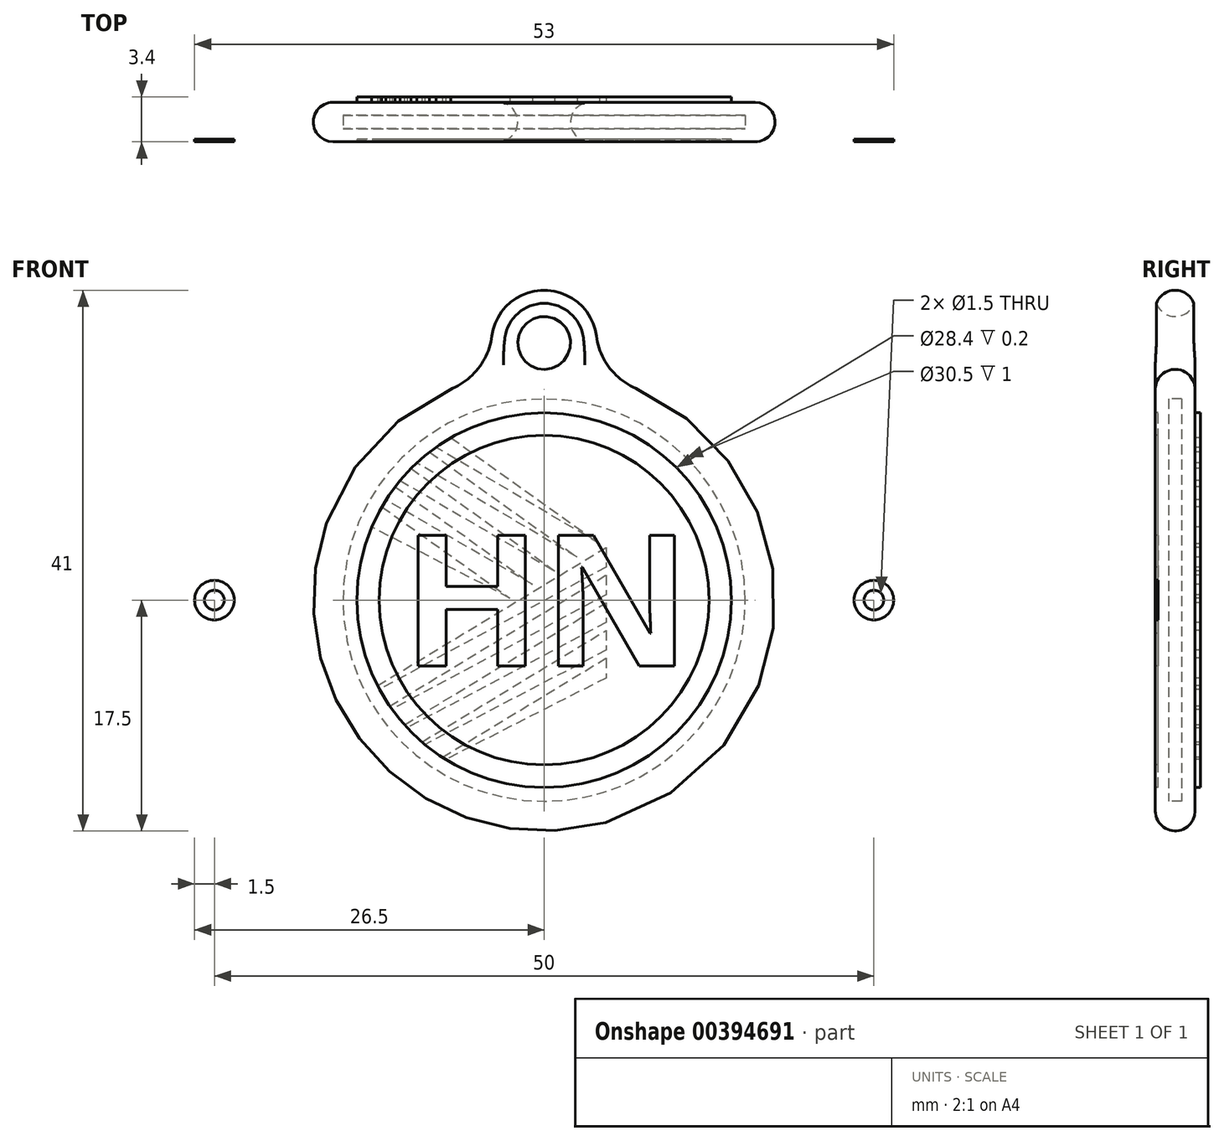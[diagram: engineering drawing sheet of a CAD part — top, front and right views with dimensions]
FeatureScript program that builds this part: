
annotation { "Feature Type Name" : "Feature", "Feature Type Description" : "" }
export const myFeature = defineFeature(function(context is Context, id is Id, definition is map)
    precondition{}
    {
        {
            var Q0;
            Q0=qCreatedBy(makeId("Front.planeOp"),FACE);
            var sketch = newSketch(context, id + "F0", { "sketchPlane" : qUnion([Q0])});
            skCircle(sketch, "E0", {"center": v(0, 0) * mm, "radius": 17.5 * mm});
            skSolve(sketch);
        }
        {
            var Q0;
            Q0 = qSketchRegion(id + "F0", true);
            extrude(context, id + "F1", {"entities" : qUnion([Q0]), "depth" : 1 * mm});
        }
        {
            var Q0;
            Q0=makeQuery(id+"F1.opExtrude","CAP_FACE",FACE,{"disambiguationData":[OSD([sQuery(id+"F0.wireOp",EDGE,"E0")])],"isStart":true});
            var sketch = newSketch(context, id + "F2", { "sketchPlane" : qUnion([Q0])});
            skCircle(sketch, "E1", {"center": v(0, 0) * mm, "radius": 17.5 * mm});
            skCircle(sketch, "E2", {"center": v(0, 0) * mm, "radius": 15.25 * mm});
            skSolve(sketch);
        }
        {
            var Q0;
            Q0 = qSketchRegion(id + "F2", true);
            extrude(context, id + "F3", {"entities" : qUnion([Q0]), "operationType" : NewBodyOperationType.ADD, "depth" : 1 * mm});
        }
        {
            var Q0;
            Q0=makeQuery(id+"F3.opExtrude","CAP_FACE",FACE,{"disambiguationData":[OSD([sQuery(id+"F2.wireOp",EDGE,"E1"),sQuery(id+"F2.wireOp",EDGE,"E2")])],"isStart":false});
            var sketch = newSketch(context, id + "F4", { "sketchPlane" : qUnion([Q0])});
            skCircle(sketch, "E3", {"center": v(0, 0) * mm, "radius": 17.5 * mm});
            skSolve(sketch);
        }
        {
            var Q0;
            Q0 = qSketchRegion(id + "F4", true);
            extrude(context, id + "F5", {"entities" : qUnion([Q0]), "operationType" : NewBodyOperationType.ADD, "depth" : 1 * mm});
        }
        {
            var Q0;
            Q0=makeQuery(id+"F1.opExtrude","CAP_FACE",FACE,{"disambiguationData":[OSD([sQuery(id+"F0.wireOp",EDGE,"E0")])],"isStart":false});
            var sketch = newSketch(context, id + "F6", { "sketchPlane" : qUnion([Q0])});
            skText(sketch, "E4", { "text": "HN", "fontName": "OpenSans-Bold.ttf"});
            skCircle(sketch, "E5", {"center": v(0, 0) * mm, "radius": 12.5 * mm});
            skCircle(sketch, "E6", {"center": v(0, 0) * mm, "radius": 14.2 * mm});
            const initialGuessF6  = {"E4": [-0.01079, -0.005, 1, 0, 0.01]};
            skSetInitialGuess(sketch, initialGuessF6);
            skSolve(sketch);
        }
        {
            var Q0;
            Q0=makeQuery(id+"F6.imprint","IMPRINT",FACE,{"disambiguationData":[TD([[makeQuery(id+"F6.imprint","IMPRINT",EDGE,{"derivedFrom":sQuery(id+"F6.wireOp",EDGE,"E5")}),-1.0]])]});
            var Q1;
            Q1=makeQuery(id+"F6.imprint","IMPRINT",FACE,{"disambiguationData":[TD([[makeQuery(id+"F6.imprint","IMPRINT",EDGE,{"derivedFrom":sQuery(id+"F6.wireOp",EDGE,"E4.sketch_text.stroke-0")}),-1.0]])]});
            var Q2;
            Q2=makeQuery(id+"F6.imprint","IMPRINT",FACE,{"disambiguationData":[TD([[makeQuery(id+"F6.imprint","IMPRINT",EDGE,{"derivedFrom":sQuery(id+"F6.wireOp",EDGE,"E4.sketch_text.stroke-12")}),-1.0]])]});
            var Q3;
            Q3=makeQuery(id+"F6.imprint","IMPRINT",FACE,{"disambiguationData":[TD([[makeQuery(id+"F6.imprint","IMPRINT",EDGE,{"derivedFrom":sQuery(id+"F6.wireOp",EDGE,"E4.sketch_text.stroke-20")}),-1.0]])]});
            var Q4;
            Q4=makeQuery(id+"F6.imprint","IMPRINT",FACE,{"disambiguationData":[TD([[makeQuery(id+"F6.imprint","IMPRINT",EDGE,{"derivedFrom":sQuery(id+"F6.wireOp",EDGE,"E4.sketch_text.stroke-34")}),-1.0]])]});
            var Q5;
            Q5=makeQuery(id+"F6.imprint","IMPRINT",FACE,{"disambiguationData":[TD([[makeQuery(id+"F6.imprint","IMPRINT",EDGE,{"derivedFrom":sQuery(id+"F6.wireOp",EDGE,"2f791306-b3d7-45ab-86ae-8695a74e6aea.sketch_text.stroke-0")}),-1.0]])]});
            var Q6;
            Q6=makeQuery(id+"F6.imprint","IMPRINT",FACE,{"disambiguationData":[TD([[makeQuery(id+"F6.imprint","IMPRINT",EDGE,{"derivedFrom":sQuery(id+"F6.wireOp",EDGE,"2f791306-b3d7-45ab-86ae-8695a74e6aea.sketch_text.stroke-10")}),-1.0]])]});
            var Q7;
            Q7=makeQuery(id+"F6.imprint","IMPRINT",FACE,{"disambiguationData":[TD([[makeQuery(id+"F6.imprint","IMPRINT",EDGE,{"derivedFrom":sQuery(id+"F6.wireOp",EDGE,"2f791306-b3d7-45ab-86ae-8695a74e6aea.sketch_text.stroke-14")}),-1.0]])]});
            var Q8;
            Q8=makeQuery(id+"F6.imprint","IMPRINT",FACE,{"disambiguationData":[TD([[makeQuery(id+"F6.imprint","IMPRINT",EDGE,{"derivedFrom":sQuery(id+"F6.wireOp",EDGE,"2f791306-b3d7-45ab-86ae-8695a74e6aea.sketch_text.stroke-30")}),-1.0]])]});
            extrude(context, id + "F7", {"entities" : qUnion([Q0, Q1, Q2, Q3, Q4, Q5, Q6, Q7, Q8]), "operationType" : NewBodyOperationType.REMOVE, "oppositeDirection" : true, "depth" : 0.2 * mm});
        }
        {
            var Q0;
            Q0=makeQuery(id+"F7.boolean.opBoolean","COPY",FACE,{"derivedFrom":makeQuery(id+"F7.opExtrude","CAP_FACE",FACE,{"disambiguationData":[OSD([sQuery(id+"F6.wireOp",EDGE,"E5"),sQuery(id+"F6.wireOp",EDGE,"E6")])],"isStart":false})});
            var sketch = newSketch(context, id + "F8", { "sketchPlane" : qUnion([Q0])});
            skCircle(sketch, "E7", {"center": v(0, 0) * mm, "radius": 16.5 * mm});
            skCircle(sketch, "E8", {"center": v(0, 0) * mm, "radius": 15 * mm});
            skText(sketch, "E9", { "text": "VIP", "fontName": "OpenSans-Bold.ttf"});
            skText(sketch, "E10", { "text": "H.N.", "fontName": "OpenSans-Bold.ttf"});
            const initialGuessF8  = {"E9": [-0.00735, 0.0025, 1, 0, 0.0065], "E10": [-0.00973, -0.009, 1, 0, 0.0065]};
            skSetInitialGuess(sketch, initialGuessF8);
            skSolve(sketch);
        }
        {
            var Q0;
            Q0=makeQuery(id+"F8.imprint","IMPRINT",FACE,{"disambiguationData":[TD([[makeQuery(id+"F8.imprint","IMPRINT",EDGE,{"derivedFrom":sQuery(id+"F8.wireOp",EDGE,"E9.sketch_text.stroke-0")}),-1.0]])]});
            var Q1;
            Q1=makeQuery(id+"F8.imprint","IMPRINT",FACE,{"disambiguationData":[TD([[makeQuery(id+"F8.imprint","IMPRINT",EDGE,{"derivedFrom":sQuery(id+"F8.wireOp",EDGE,"E9.sketch_text.stroke-10")}),-1.0]])]});
            var Q2;
            Q2=makeQuery(id+"F8.imprint","IMPRINT",FACE,{"disambiguationData":[TD([[makeQuery(id+"F8.imprint","IMPRINT",EDGE,{"derivedFrom":sQuery(id+"F8.wireOp",EDGE,"E9.sketch_text.stroke-14")}),-1.0]])]});
            var Q3;
            Q3=makeQuery(id+"F8.imprint","IMPRINT",FACE,{"disambiguationData":[TD([[makeQuery(id+"F8.imprint","IMPRINT",EDGE,{"derivedFrom":sQuery(id+"F8.wireOp",EDGE,"E9.sketch_text.stroke-30")}),-1.0]])]});
            var Q4;
            Q4=makeQuery(id+"F8.imprint","IMPRINT",FACE,{"disambiguationData":[TD([[makeQuery(id+"F8.imprint","IMPRINT",EDGE,{"derivedFrom":sQuery(id+"F8.wireOp",EDGE,"E10.sketch_text.stroke-0")}),-1.0]])]});
            var Q5;
            Q5=makeQuery(id+"F8.imprint","IMPRINT",FACE,{"disambiguationData":[TD([[makeQuery(id+"F8.imprint","IMPRINT",EDGE,{"derivedFrom":sQuery(id+"F8.wireOp",EDGE,"E10.sketch_text.stroke-12")}),-1.0]])]});
            var Q6;
            Q6=makeQuery(id+"F8.imprint","IMPRINT",FACE,{"disambiguationData":[TD([[makeQuery(id+"F8.imprint","IMPRINT",EDGE,{"derivedFrom":sQuery(id+"F8.wireOp",EDGE,"E10.sketch_text.stroke-20")}),-1.0]])]});
            var Q7;
            Q7=makeQuery(id+"F8.imprint","IMPRINT",FACE,{"disambiguationData":[TD([[makeQuery(id+"F8.imprint","IMPRINT",EDGE,{"derivedFrom":sQuery(id+"F8.wireOp",EDGE,"E10.sketch_text.stroke-34")}),-1.0]])]});
            var Q8;
            Q8=makeQuery(id+"F8.imprint","IMPRINT",FACE,{"disambiguationData":[TD([[makeQuery(id+"F8.imprint","IMPRINT",EDGE,{"derivedFrom":sQuery(id+"F8.wireOp",EDGE,"E7")}),1.0]])]});
            extrude(context, id + "F9", {"entities" : qUnion([Q0, Q1, Q2, Q3, Q4, Q5, Q6, Q7, Q8]), "depth" : 0.2 * mm});
        }
        {
            var Q0;
            Q0=makeQuery(id+"Fh8yMcBjIkPt4Dr_11.boolean.opBoolean","MERGE",FACE,{"derivedFrom":[makeQuery(id+"F5.opExtrude","CAP_FACE",FACE,{"disambiguationData":[OSD([sQuery(id+"F4.wireOp",EDGE,"E3")])],"isStart":false}),makeQuery(id+"Fh8yMcBjIkPt4Dr_11.opExtrude","CAP_FACE",FACE,{"disambiguationData":[OSD([sQuery(id+"FN8h1bw3wlibMYA_11.wireOp",EDGE,"BS7OUwbq-2ru2-1JD7-GIha-xYvTOZTgPK9A"),sQuery(id+"FN8h1bw3wlibMYA_11.wireOp",EDGE,"aJaIA7Kc-m8c6-AEcG-Va6J-VanrhZFaR41i")])],"isStart":false})]});
            var sketch = newSketch(context, id + "F10", { "sketchPlane" : qUnion([Q0])});
            skArc(sketch, "E11", {"start": v(12.63, -6.5) * mm, "mid": v(14.2, -0.52) * mm, "end": v(13.07, 5.55) * mm});
            skLineSegment(sketch, "E12", {"start": v(12.63, -6.5) * mm, "end": v(-4.7, 4) * mm});
            skLineSegment(sketch, "E13", {"start": v(-4.7, 4) * mm, "end": v(-4.7, 2.5) * mm});
            skLineSegment(sketch, "E14", {"start": v(-4.7, 2.5) * mm, "end": v(12.49, -6.76) * mm});
            skLineSegment(sketch, "E15", {"start": v(-4.7, 1.9) * mm, "end": v(-4.7, 0.4) * mm});
            skLineSegment(sketch, "E16", {"start": v(-4.7, 0.4) * mm, "end": v(11.53, -8.28) * mm});
            skLineSegment(sketch, "E17", {"start": v(11.7, -8.04) * mm, "end": v(-4.7, 1.9) * mm});
            skLineSegment(sketch, "E18", {"start": v(-4.7, -0.2) * mm, "end": v(-4.7, -1.7) * mm});
            skLineSegment(sketch, "E19", {"start": v(-4.7, -1.7) * mm, "end": v(10.39, -9.68) * mm});
            skLineSegment(sketch, "E20", {"start": v(10.6, -9.46) * mm, "end": v(-4.7, -0.2) * mm});
            skLineSegment(sketch, "E21", {"start": v(-4.7, -2.3) * mm, "end": v(-4.7, -3.8) * mm});
            skLineSegment(sketch, "E22", {"start": v(-4.7, -3.8) * mm, "end": v(9.04, -10.95) * mm});
            skLineSegment(sketch, "E23", {"start": v(9.27, -10.76) * mm, "end": v(-4.7, -2.3) * mm});
            skLineSegment(sketch, "E24", {"start": v(-4.7, -4.4) * mm, "end": v(-4.7, -5.9) * mm});
            skLineSegment(sketch, "E25", {"start": v(-4.7, -5.9) * mm, "end": v(7.46, -12.08) * mm});
            skLineSegment(sketch, "E26", {"start": v(7.72, -11.92) * mm, "end": v(-4.7, -4.4) * mm});
            skArc(sketch, "E27.trimOffspring", {"start": v(11.7, -8.04) * mm, "mid": v(12.11, -7.4) * mm, "end": v(12.49, -6.76) * mm});
            skArc(sketch, "E28.trimOffspring", {"start": v(10.6, -9.46) * mm, "mid": v(11.08, -8.88) * mm, "end": v(11.53, -8.28) * mm});
            skArc(sketch, "E29.trimOffspring", {"start": v(9.27, -10.76) * mm, "mid": v(9.84, -10.24) * mm, "end": v(10.39, -9.68) * mm});
            skArc(sketch, "E30.trimOffspring", {"start": v(7.72, -11.92) * mm, "mid": v(8.4, -11.46) * mm, "end": v(9.04, -10.95) * mm});
            skLineSegment(sketch, "E31", {"start": v(7.07, 12.32) * mm, "end": v(-4.2, 4.28) * mm});
            skLineSegment(sketch, "E32", {"start": v(-4.2, 4.28) * mm, "end": v(8.2, 11.59) * mm});
            skLineSegment(sketch, "E33", {"start": v(8.69, 11.23) * mm, "end": v(-2.5, 3.25) * mm});
            skLineSegment(sketch, "E34", {"start": v(-2.5, 3.25) * mm, "end": v(9.66, 10.4) * mm});
            skLineSegment(sketch, "E35", {"start": v(10.1, 10) * mm, "end": v(-0.8, 2.22) * mm});
            skLineSegment(sketch, "E36", {"start": v(11.3, 8.6) * mm, "end": v(0.9, 1.2) * mm});
            skLineSegment(sketch, "E37", {"start": v(0.9, 1.2) * mm, "end": v(12, 7.6) * mm});
            skLineSegment(sketch, "E38", {"start": v(12.3, 7.09) * mm, "end": v(2.6, 0.16) * mm});
            skLineSegment(sketch, "E39", {"start": v(2.6, 0.16) * mm, "end": v(13.07, 5.55) * mm});
            skArc(sketch, "E40.trimOffspring", {"start": v(7.07, 12.32) * mm, "mid": v(-14.2, -0.23) * mm, "end": v(7.46, -12.08) * mm});
            skArc(sketch, "E41.trimOffspring", {"start": v(8.69, 11.23) * mm, "mid": v(8.45, 11.41) * mm, "end": v(8.2, 11.59) * mm});
            skArc(sketch, "E42.trimOffspring", {"start": v(10.1, 10) * mm, "mid": v(9.88, 10.2) * mm, "end": v(9.66, 10.4) * mm});
            skArc(sketch, "E43.trimOffspring", {"start": v(11.3, 8.6) * mm, "mid": v(11.1, 8.84) * mm, "end": v(10.92, 9.08) * mm});
            skArc(sketch, "E44.trimOffspring", {"start": v(12.3, 7.09) * mm, "mid": v(12.15, 7.34) * mm, "end": v(12, 7.6) * mm});
            skLineSegment(sketch, "E45", {"start": v(10.92, 9.08) * mm, "end": v(-0.8, 2.22) * mm});
            skSolve(sketch);
        }
        {
            var Q0;
            Q0 = qSketchRegion(id + "F10", true);
            extrude(context, id + "F11", {"entities" : qUnion([Q0]), "operationType" : NewBodyOperationType.ADD, "depth" : 0.4 * mm});
        }
        {
            var Q0;
            Q0=makeQuery(id+"F9.opExtrude","SWEPT_BODY",BODY,{"disambiguationData":[OSD([sQuery(id+"F8.wireOp",EDGE,"E7"),sQuery(id+"F8.wireOp",EDGE,"E8")])]});
            var Q1;
            Q1=makeQuery(id+"F9.opExtrude","SWEPT_BODY",BODY,{"disambiguationData":[OSD([sQuery(id+"F8.wireOp",EDGE,"E9.sketch_text.stroke-0"),sQuery(id+"F8.wireOp",EDGE,"E9.sketch_text.stroke-1"),sQuery(id+"F8.wireOp",EDGE,"E9.sketch_text.stroke-2"),sQuery(id+"F8.wireOp",EDGE,"E9.sketch_text.stroke-3"),sQuery(id+"F8.wireOp",EDGE,"E9.sketch_text.stroke-4"),sQuery(id+"F8.wireOp",EDGE,"E9.sketch_text.stroke-5"),sQuery(id+"F8.wireOp",EDGE,"E9.sketch_text.stroke-6"),sQuery(id+"F8.wireOp",EDGE,"E9.sketch_text.stroke-7"),sQuery(id+"F8.wireOp",EDGE,"E9.sketch_text.stroke-8"),sQuery(id+"F8.wireOp",EDGE,"E9.sketch_text.stroke-9")])]});
            var Q2;
            Q2=makeQuery(id+"F9.opExtrude","SWEPT_BODY",BODY,{"disambiguationData":[OSD([sQuery(id+"F8.wireOp",EDGE,"E9.sketch_text.stroke-14"),sQuery(id+"F8.wireOp",EDGE,"E9.sketch_text.stroke-15"),sQuery(id+"F8.wireOp",EDGE,"E9.sketch_text.stroke-16"),sQuery(id+"F8.wireOp",EDGE,"E9.sketch_text.stroke-17"),sQuery(id+"F8.wireOp",EDGE,"E9.sketch_text.stroke-18"),sQuery(id+"F8.wireOp",EDGE,"E9.sketch_text.stroke-19"),sQuery(id+"F8.wireOp",EDGE,"E9.sketch_text.stroke-20"),sQuery(id+"F8.wireOp",EDGE,"E9.sketch_text.stroke-21"),sQuery(id+"F8.wireOp",EDGE,"E9.sketch_text.stroke-22"),sQuery(id+"F8.wireOp",EDGE,"E9.sketch_text.stroke-23"),sQuery(id+"F8.wireOp",EDGE,"E9.sketch_text.stroke-24"),sQuery(id+"F8.wireOp",EDGE,"E9.sketch_text.stroke-25"),sQuery(id+"F8.wireOp",EDGE,"E9.sketch_text.stroke-26"),sQuery(id+"F8.wireOp",EDGE,"E9.sketch_text.stroke-27"),sQuery(id+"F8.wireOp",EDGE,"E9.sketch_text.stroke-28"),sQuery(id+"F8.wireOp",EDGE,"E9.sketch_text.stroke-29")])]});
            var Q3;
            Q3=makeQuery(id+"F9.opExtrude","SWEPT_BODY",BODY,{"disambiguationData":[OSD([sQuery(id+"F8.wireOp",EDGE,"E10.sketch_text.stroke-34"),sQuery(id+"F8.wireOp",EDGE,"E10.sketch_text.stroke-35"),sQuery(id+"F8.wireOp",EDGE,"E10.sketch_text.stroke-36"),sQuery(id+"F8.wireOp",EDGE,"E10.sketch_text.stroke-37"),sQuery(id+"F8.wireOp",EDGE,"E10.sketch_text.stroke-38"),sQuery(id+"F8.wireOp",EDGE,"E10.sketch_text.stroke-39"),sQuery(id+"F8.wireOp",EDGE,"E10.sketch_text.stroke-40"),sQuery(id+"F8.wireOp",EDGE,"E10.sketch_text.stroke-41")])]});
            var Q4;
            Q4=makeQuery(id+"F9.opExtrude","SWEPT_BODY",BODY,{"disambiguationData":[OSD([sQuery(id+"F8.wireOp",EDGE,"E10.sketch_text.stroke-0"),sQuery(id+"F8.wireOp",EDGE,"E10.sketch_text.stroke-1"),sQuery(id+"F8.wireOp",EDGE,"E10.sketch_text.stroke-2"),sQuery(id+"F8.wireOp",EDGE,"E10.sketch_text.stroke-3"),sQuery(id+"F8.wireOp",EDGE,"E10.sketch_text.stroke-4"),sQuery(id+"F8.wireOp",EDGE,"E10.sketch_text.stroke-5"),sQuery(id+"F8.wireOp",EDGE,"E10.sketch_text.stroke-6"),sQuery(id+"F8.wireOp",EDGE,"E10.sketch_text.stroke-7"),sQuery(id+"F8.wireOp",EDGE,"E10.sketch_text.stroke-8"),sQuery(id+"F8.wireOp",EDGE,"E10.sketch_text.stroke-9"),sQuery(id+"F8.wireOp",EDGE,"E10.sketch_text.stroke-10"),sQuery(id+"F8.wireOp",EDGE,"E10.sketch_text.stroke-11")])]});
            deleteBodies(context, id + "F12", {"entities" : qUnion([Q0, Q1, Q2, Q3, Q4])});
        }
        {
            var Q0;
            Q0=makeQuery(id+"F9.opExtrude","SWEPT_BODY",BODY,{"disambiguationData":[OSD([sQuery(id+"F8.wireOp",EDGE,"E9.sketch_text.stroke-10"),sQuery(id+"F8.wireOp",EDGE,"E9.sketch_text.stroke-11"),sQuery(id+"F8.wireOp",EDGE,"E9.sketch_text.stroke-12"),sQuery(id+"F8.wireOp",EDGE,"E9.sketch_text.stroke-13")])]});
            var Q1;
            Q1=makeQuery(id+"F9.opExtrude","SWEPT_BODY",BODY,{"disambiguationData":[OSD([sQuery(id+"F8.wireOp",EDGE,"E10.sketch_text.stroke-12"),sQuery(id+"F8.wireOp",EDGE,"E10.sketch_text.stroke-13"),sQuery(id+"F8.wireOp",EDGE,"E10.sketch_text.stroke-14"),sQuery(id+"F8.wireOp",EDGE,"E10.sketch_text.stroke-15"),sQuery(id+"F8.wireOp",EDGE,"E10.sketch_text.stroke-16"),sQuery(id+"F8.wireOp",EDGE,"E10.sketch_text.stroke-17"),sQuery(id+"F8.wireOp",EDGE,"E10.sketch_text.stroke-18"),sQuery(id+"F8.wireOp",EDGE,"E10.sketch_text.stroke-19")])]});
            deleteBodies(context, id + "F13", {"entities" : qUnion([Q0, Q1])});
        }
        {
            var Q0;
            Q0=makeQuery(id+"F9.opExtrude","SWEPT_BODY",BODY,{"disambiguationData":[OSD([sQuery(id+"F8.wireOp",EDGE,"E10.sketch_text.stroke-20"),sQuery(id+"F8.wireOp",EDGE,"E10.sketch_text.stroke-21"),sQuery(id+"F8.wireOp",EDGE,"E10.sketch_text.stroke-22"),sQuery(id+"F8.wireOp",EDGE,"E10.sketch_text.stroke-23"),sQuery(id+"F8.wireOp",EDGE,"E10.sketch_text.stroke-24"),sQuery(id+"F8.wireOp",EDGE,"E10.sketch_text.stroke-25"),sQuery(id+"F8.wireOp",EDGE,"E10.sketch_text.stroke-26"),sQuery(id+"F8.wireOp",EDGE,"E10.sketch_text.stroke-27"),sQuery(id+"F8.wireOp",EDGE,"E10.sketch_text.stroke-28"),sQuery(id+"F8.wireOp",EDGE,"E10.sketch_text.stroke-29"),sQuery(id+"F8.wireOp",EDGE,"E10.sketch_text.stroke-30"),sQuery(id+"F8.wireOp",EDGE,"E10.sketch_text.stroke-31"),sQuery(id+"F8.wireOp",EDGE,"E10.sketch_text.stroke-32"),sQuery(id+"F8.wireOp",EDGE,"E10.sketch_text.stroke-33")])]});
            deleteBodies(context, id + "F14", {"entities" : qUnion([Q0])});
        }
        {
            var Q0;
            {var subQ0=sQuery(id+"F0.wireOp",EDGE,"E0");Q0=makeQuery(id+"F7.boolean.opBoolean","SPLIT",FACE,{"disambiguationData":[TD([makeQuery(id+"F1.opExtrude","SWEPT_FACE",FACE,{"disambiguationData":[OSD([subQ0])]})])],"derivedFrom":makeQuery(id+"F1.opExtrude","CAP_FACE",FACE,{"disambiguationData":[OSD([subQ0])],"isStart":false})});}
            var sketch = newSketch(context, id + "F15", { "sketchPlane" : qUnion([Q0])});
            skCircle(sketch, "E46", {"center": v(0, 19.5) * mm, "radius": 2 * mm});
            skCircle(sketch, "E47", {"center": v(0, 19.5) * mm, "radius": 4 * mm});
            skSolve(sketch);
        }
        {
            var Q0;
            Q0 = qSketchRegion(id + "F15", true);
            var Q1;
            Q1=makeQuery(id+"F5.opExtrude","CAP_FACE",FACE,{"disambiguationData":[OSD([sQuery(id+"F4.wireOp",EDGE,"E3")])],"isStart":false});
            extrude(context, id + "F16", {"entities" : qUnion([Q0]), "operationType" : NewBodyOperationType.ADD, "endBound" : BoundingType.UP_TO_SURFACE, "oppositeDirection" : true, "endBoundEntityFace" : qUnion([Q1]), "depth" : 25 * mm});
        }
        {
            var Q0;
            Q0=makeQuery(id+"F16.boolean.opBoolean","INTERSECT",EDGE,{"disambiguationData":[OD(0.0)],"derivedFrom":[makeQuery(id+"F5.boolean.opBoolean","MERGE",FACE,{"derivedFrom":[makeQuery(id+"F3.boolean.opBoolean","MERGE",FACE,{"derivedFrom":[makeQuery(id+"F1.opExtrude","SWEPT_FACE",FACE,{"disambiguationData":[OSD([sQuery(id+"F0.wireOp",EDGE,"E0")])]}),makeQuery(id+"F3.opExtrude","SWEPT_FACE",FACE,{"disambiguationData":[OSD([sQuery(id+"F2.wireOp",EDGE,"E1")])]})]}),makeQuery(id+"F5.opExtrude","SWEPT_FACE",FACE,{"disambiguationData":[OSD([sQuery(id+"F4.wireOp",EDGE,"E3")])]})]}),makeQuery(id+"F16.opExtrude","SWEPT_FACE",FACE,{"disambiguationData":[OSD([sQuery(id+"F15.wireOp",EDGE,"E47")])]})]});
            var Q1;
            Q1=makeQuery(id+"F16.boolean.opBoolean","INTERSECT",EDGE,{"disambiguationData":[OD(1.0)],"derivedFrom":[makeQuery(id+"F5.boolean.opBoolean","MERGE",FACE,{"derivedFrom":[makeQuery(id+"F3.boolean.opBoolean","MERGE",FACE,{"derivedFrom":[makeQuery(id+"F1.opExtrude","SWEPT_FACE",FACE,{"disambiguationData":[OSD([sQuery(id+"F0.wireOp",EDGE,"E0")])]}),makeQuery(id+"F3.opExtrude","SWEPT_FACE",FACE,{"disambiguationData":[OSD([sQuery(id+"F2.wireOp",EDGE,"E1")])]})]}),makeQuery(id+"F5.opExtrude","SWEPT_FACE",FACE,{"disambiguationData":[OSD([sQuery(id+"F4.wireOp",EDGE,"E3")])]})]}),makeQuery(id+"F16.opExtrude","SWEPT_FACE",FACE,{"disambiguationData":[OSD([sQuery(id+"F15.wireOp",EDGE,"E47")])]})]});
            fillet(context, id + "F17", {"entities" : qUnion([Q0, Q1]), "radius" : 5 * mm, "tangentPropagation" : true, "allowEdgeOverflow" : false});
        }
        {
            var Q0;
            Q0=makeQuery(id+"F1.opExtrude","CAP_EDGE",EDGE,{"disambiguationData":[OSD([sQuery(id+"F0.wireOp",EDGE,"E0")])],"isStart":false});
            var Q1;
            {var subQ0=sQuery(id+"F15.wireOp",EDGE,"E47");var subQ1=sQuery(id+"F4.wireOp",EDGE,"E3");Q1=makeQuery(id+"F17.opFillet","BLEND_EDGE",EDGE,{"blendedFrom":[makeQuery(id+"F16.boolean.opBoolean","INTERSECT",EDGE,{"disambiguationData":[OD(0.0)],"derivedFrom":[makeQuery(id+"F5.boolean.opBoolean","MERGE",FACE,{"derivedFrom":[makeQuery(id+"F3.boolean.opBoolean","MERGE",FACE,{"derivedFrom":[makeQuery(id+"F1.opExtrude","SWEPT_FACE",FACE,{"disambiguationData":[OSD([sQuery(id+"F0.wireOp",EDGE,"E0")])]}),makeQuery(id+"F3.opExtrude","SWEPT_FACE",FACE,{"disambiguationData":[OSD([sQuery(id+"F2.wireOp",EDGE,"E1")])]})]}),makeQuery(id+"F5.opExtrude","SWEPT_FACE",FACE,{"disambiguationData":[OSD([subQ1])]})]}),makeQuery(id+"F16.opExtrude","SWEPT_FACE",FACE,{"disambiguationData":[OSD([subQ0])]})]}),makeQuery(id+"F16.boolean.opBoolean","MERGE",FACE,{"derivedFrom":[makeQuery(id+"F5.opExtrude","CAP_FACE",FACE,{"disambiguationData":[OSD([subQ1])],"isStart":false}),makeQuery(id+"F16.opExtrude","CAP_FACE",FACE,{"disambiguationData":[OSD([sQuery(id+"F15.wireOp",EDGE,"E46"),subQ0])],"isStart":false})]})],"blendedInto":[makeQuery(id+"F16.boolean.opBoolean","MERGE",FACE,{"derivedFrom":[makeQuery(id+"F5.opExtrude","CAP_FACE",FACE,{"disambiguationData":[OSD([subQ1])],"isStart":false}),makeQuery(id+"F16.opExtrude","CAP_FACE",FACE,{"disambiguationData":[OSD([sQuery(id+"F15.wireOp",EDGE,"E46"),subQ0])],"isStart":false})]})]});}
            var Q2;
            Q2=makeQuery(id+"F16.opExtrude","CAP_EDGE",EDGE,{"disambiguationData":[OSD([sQuery(id+"F15.wireOp",EDGE,"E46")])],"isStart":true});
            var Q3;
            Q3=makeQuery(id+"F16.opExtrude","CAP_EDGE",EDGE,{"disambiguationData":[OSD([sQuery(id+"F15.wireOp",EDGE,"E46")])],"isStart":false});
            fillet(context, id + "F18", {"entities" : qUnion([Q0, Q1, Q2, Q3]), "radius" : 1.5 * mm, "tangentPropagation" : true, "allowEdgeOverflow" : false});
        }
        {
            var Q0;
            {var subQ0=sQuery(id+"F0.wireOp",EDGE,"E0");Q0=makeQuery(id+"F16.boolean.opBoolean","MERGE",FACE,{"derivedFrom":[makeQuery(id+"F7.boolean.opBoolean","SPLIT",FACE,{"disambiguationData":[TD([makeQuery(id+"F1.opExtrude","SWEPT_FACE",FACE,{"disambiguationData":[OSD([subQ0])]})])],"derivedFrom":makeQuery(id+"F1.opExtrude","CAP_FACE",FACE,{"disambiguationData":[OSD([subQ0])],"isStart":false})}),makeQuery(id+"F16.opExtrude","CAP_FACE",FACE,{"disambiguationData":[OSD([sQuery(id+"F15.wireOp",EDGE,"E46"),sQuery(id+"F15.wireOp",EDGE,"E47")])],"isStart":true})]});}
            var sketch = newSketch(context, id + "F19", { "sketchPlane" : qUnion([Q0])});
            skCircle(sketch, "E48", {"center": v(-25, 0) * mm, "radius": 1.5 * mm});
            skCircle(sketch, "E49", {"center": v(25, 0) * mm, "radius": 1.5 * mm});
            skCircle(sketch, "E50", {"center": v(25, 0) * mm, "radius": 0.75 * mm});
            skCircle(sketch, "E51", {"center": v(-25, 0) * mm, "radius": 0.75 * mm});
            skSolve(sketch);
        }
        {
            var Q0;
            Q0 = qSketchRegion(id + "F19", true);
            extrude(context, id + "F20", {"entities" : qUnion([Q0]), "oppositeDirection" : true, "depth" : 0.2 * mm});
        }
    });
